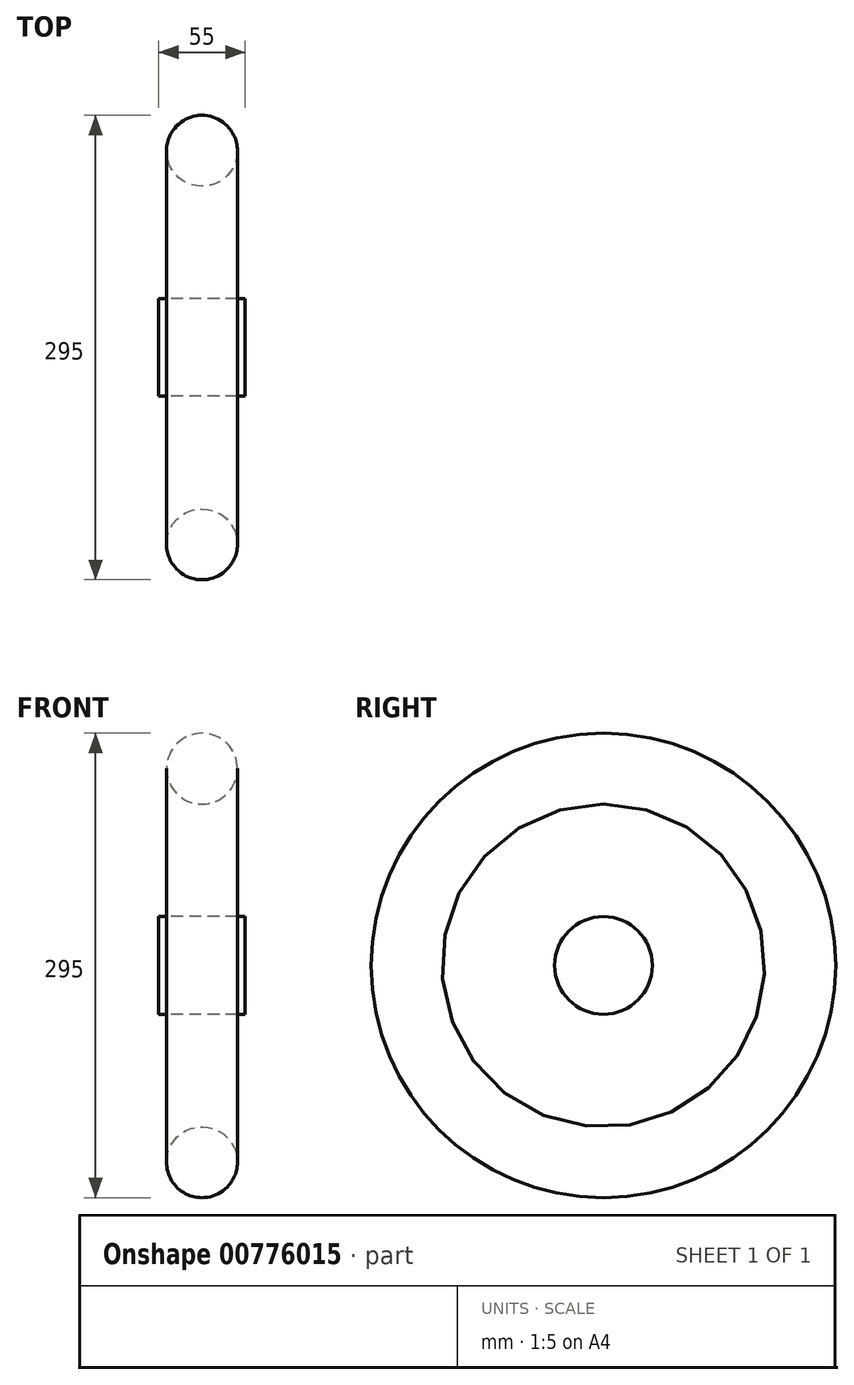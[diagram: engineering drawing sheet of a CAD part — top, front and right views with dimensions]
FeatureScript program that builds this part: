
annotation { "Feature Type Name" : "Feature", "Feature Type Description" : "" }
export const myFeature = defineFeature(function(context is Context, id is Id, definition is map)
    precondition{}
    {
        {
            var Q0;
            Q0=qCreatedBy(makeId("Front.planeOp"),FACE);
            var sketch = newSketch(context, id + "F0", { "sketchPlane" : qUnion([Q0])});
            skCircle(sketch, "E0", {"center": v(0, 125) * mm, "radius": 22.5 * mm});
            skLineSegment(sketch, "E1.bottom", {"start": v(-27.5, 31) * mm, "end": v(27.5, 31) * mm});
            skLineSegment(sketch, "E1.top", {"start": v(-27.5, 0) * mm, "end": v(27.5, 0) * mm});
            skLineSegment(sketch, "E1.left", {"start": v(-27.5, 31) * mm, "end": v(-27.5, 0) * mm});
            skLineSegment(sketch, "E1.right", {"start": v(27.5, 31) * mm, "end": v(27.5, 0) * mm});
            skSolve(sketch);
        }
        {
            var Q0;
            Q0 = qSketchRegion(id + "F0", true);
            var Q1;
            Q1=sQuery(id+"F0.wireOp",EDGE,"E1.top");
            revolve(context, id + "F1", {"surfaceOperationType" : NewSurfaceOperationType.NEW, "entities" : qUnion([Q0]), "axis" : qUnion([Q1]), "revolveType" : RevolveType.FULL});
        }
    });
